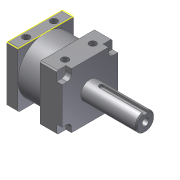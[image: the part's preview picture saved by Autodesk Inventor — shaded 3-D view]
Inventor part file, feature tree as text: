
AUTODESK INVENTOR PART (.ipt)
format: ipt  version: 2012 (Build 160160000, 160)  size: 251,904 bytes
history: native  units: in
note: dims shown in document units (in); Inventor stores cm internally (conversion verified against a paired STEP export)
features: sketch x10, extrude x9, chamfer x2, fillet x1
ambient origin geometry x8: Origin, YZ Plane, XZ Plane, XY Plane, X Axis, Y Axis, Z Axis, Center Point
bodies: Solid1 (feature_tree)
feature tree (22):
  extrude  "Extrusion1"  Depth=1.5in
  extrude  "Extrusion2"  Depth=1.5in
  sketch  "Sketch3"  dims[d5=0.75in d6=0.75in]
  extrude  "Extrusion3"  Depth=0.75in
  extrude  "Extrusion4"  Depth=1.5in
  extrude  "Extrusion5"  Depth=0.6in TaperAngle=0.0deg
  extrude  "Extrusion6"  Depth=0.75in
  extrude  "Extrusion7"  Depth=1.5in TaperAngle=0.0deg
  extrude  "Extrusion9"  Depth=0.25in
  chamfer  "Chamfer2"  Distance=0.15in
  extrude  "Extrusion10"  Depth=0.75in
  fillet  "Fillet1"  Radius=0.75in
  chamfer  "Chamfer3"  Distance=0.3in
  sketch  "Sketch1"  dims[d0=0.3in d1=1.5in]
  sketch  "Sketch2"  dims[d2=1.5in d3=0.0in d4=1.5in]
  sketch  "Sketch4"  dims[d7=0.6in d8=0.0in d9=1.5in]
  sketch  "Sketch5"  dims[d10=1.5002in d11=0.6in d12=0.0in]
  sketch  "Sketch6"  dims[d13=0.75in d14=0.75in]
  sketch  "Sketch7"  dims[d15=0.5in d16=1.5in d17=0.0in]
  sketch  "Sketch8"  dims[d18=0.25in d19=0.25in]
  sketch  "Sketch11"  dims[d20=0.125in d21=0.15in d22=0.0in]
  sketch  "Sketch12"  dims[d23=0.75in d24=0.75in d25=0.75in d26=0.3in d27=0.0in d28=0.1875in d29=0.375in d30=0.375in d31=0.15in d32=0.15in d33=0.3in d34=0.3in d35=0.375in d36=0.375in d37=0.3in d38=0.0in d48=0.125in d49=0.0625in d50=1.25in d51=0.0in d52=0.0312in d53=0.125in d54=45.0deg d55=0.1875in d56=1.0in d57=0.0in d58=0.0625in d69=0.0312in d70=0.125in d71=45.0deg]
